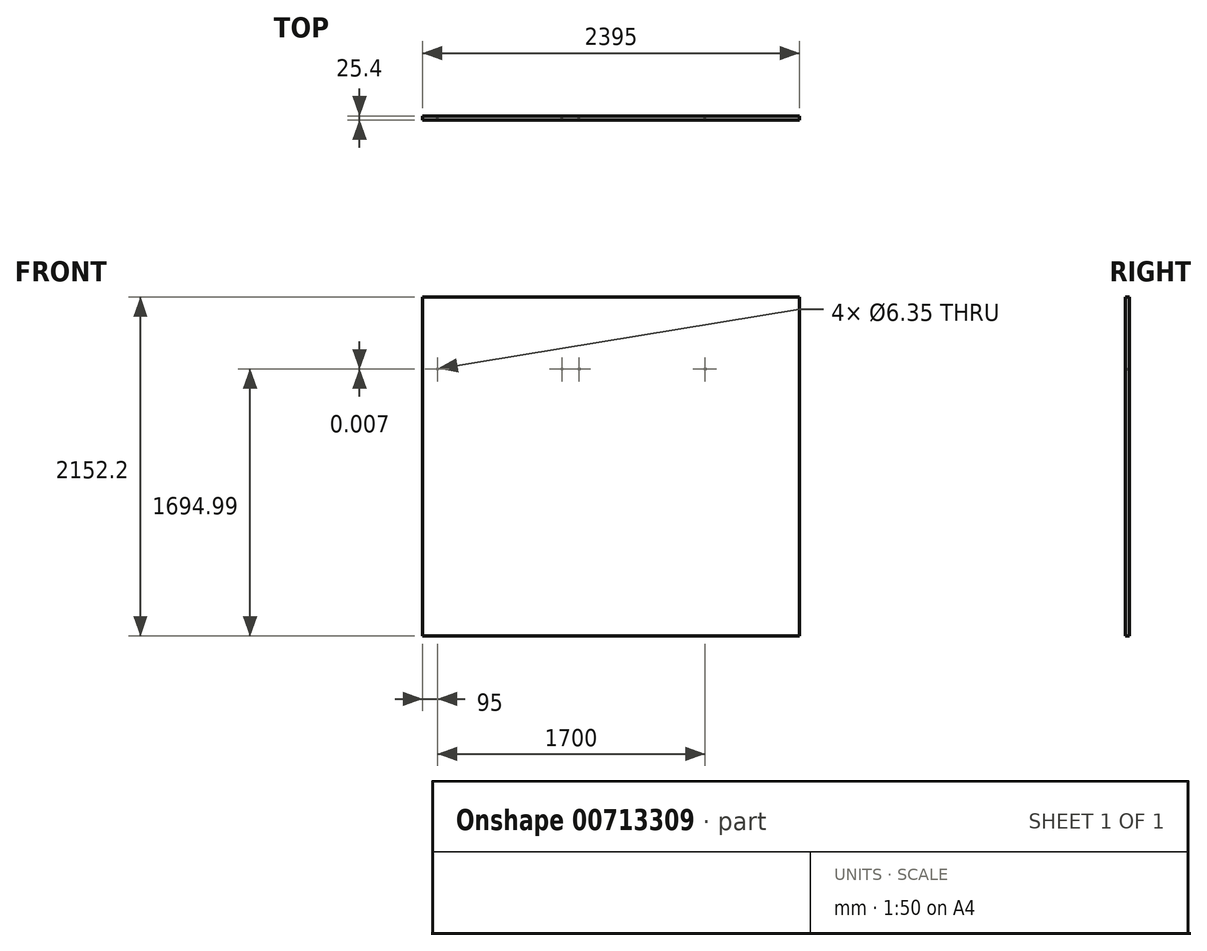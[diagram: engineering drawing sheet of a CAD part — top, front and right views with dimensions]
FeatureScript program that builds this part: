
annotation { "Feature Type Name" : "Feature", "Feature Type Description" : "" }
export const myFeature = defineFeature(function(context is Context, id is Id, definition is map)
    precondition{}
    {
        {
            var Q0;
            Q0=qCreatedBy(makeId("Front.planeOp"),FACE);
            var sketch = newSketch(context, id + "F0", { "sketchPlane" : qUnion([Q0])});
            skLineSegment(sketch, "E0.bottom", {"start": v(1197.5, -1076.1) * mm, "end": v(-1197.5, -1076.1) * mm});
            skLineSegment(sketch, "E0.top", {"start": v(1197.5, 1076.1) * mm, "end": v(-1197.5, 1076.1) * mm});
            skLineSegment(sketch, "E0.left", {"start": v(1197.5, -1076.1) * mm, "end": v(1197.5, 1076.1) * mm});
            skLineSegment(sketch, "E0.right", {"start": v(-1197.5, -1076.1) * mm, "end": v(-1197.5, 1076.1) * mm});
            skPoint(sketch, "E0.middle", {"position": v(0, 0) * mm});
            skCircle(sketch, "E1", {"center": v(-1102.5, 618.9) * mm, "radius": 3.18 * mm});
            skCircle(sketch, "E2", {"center": v(-312.5, 618.9) * mm, "radius": 3.18 * mm});
            skCircle(sketch, "E3", {"center": v(-202.5, 618.9) * mm, "radius": 3.18 * mm});
            skCircle(sketch, "E4", {"center": v(597.5, 618.9) * mm, "radius": 3.17 * mm});
            skSolve(sketch);
        }
        {
            var Q0;
            Q0=makeQuery(id+"F0.imprint","IMPRINT",FACE,{"disambiguationData":[TD([[makeQuery(id+"F0.imprint","IMPRINT",EDGE,{"derivedFrom":sQuery(id+"F0.wireOp",EDGE,"E0.bottom")}),-1.0]])]});
            extrude(context, id + "F1", {"entities" : qUnion([Q0]), "endBound" : BoundingType.SYMMETRIC, "depth" : 25.4 * mm, "offsetDistance" : 25.4 * mm});
        }
    });
